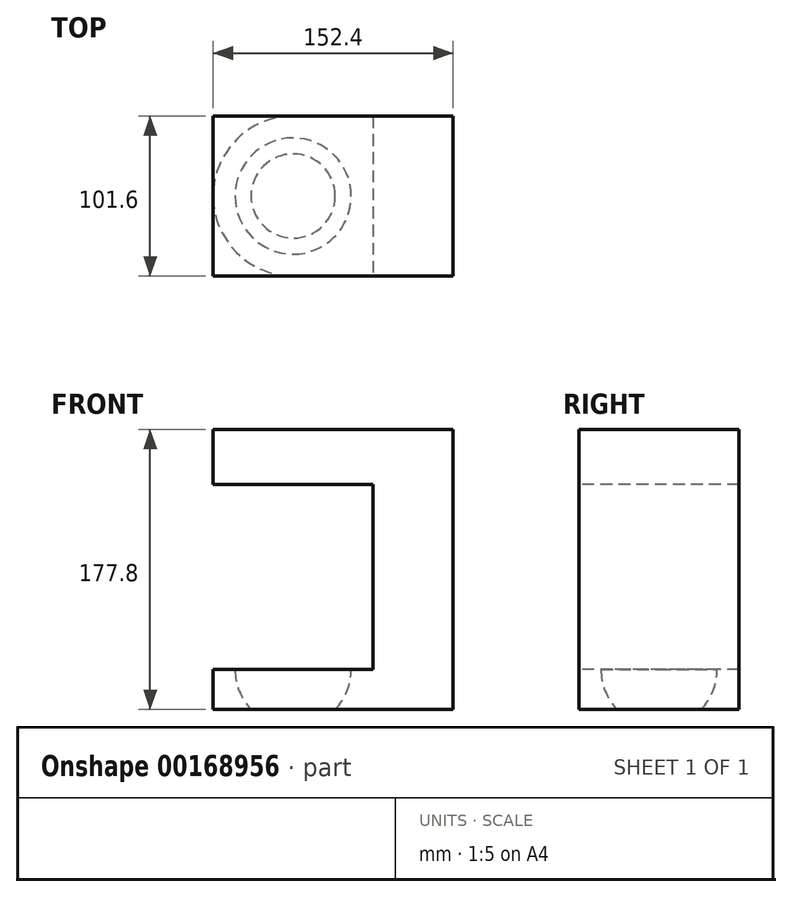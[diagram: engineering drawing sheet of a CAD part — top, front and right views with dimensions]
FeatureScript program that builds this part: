
annotation { "Feature Type Name" : "Feature", "Feature Type Description" : "" }
export const myFeature = defineFeature(function(context is Context, id is Id, definition is map)
    precondition{}
    {
        {
            var Q0;
            Q0=qCreatedBy(makeId("Top.planeOp"),FACE);
            var sketch = newSketch(context, id + "F0", { "sketchPlane" : qUnion([Q0])});
            skCircle(sketch, "E0", {"center": v(0, 0) * mm, "radius": 50.8 * mm});
            skLineSegment(sketch, "E1.bottom", {"start": v(0, 50.8) * mm, "end": v(101.6, 50.8) * mm});
            skLineSegment(sketch, "E1.top", {"start": v(0, -50.8) * mm, "end": v(101.6, -50.8) * mm});
            skLineSegment(sketch, "E1.left", {"start": v(0, 50.8) * mm, "end": v(0, -50.8) * mm});
            skLineSegment(sketch, "E1.right", {"start": v(101.6, 50.8) * mm, "end": v(101.6, -50.8) * mm});
            skSolve(sketch);
        }
        {
            var Q0;
            {var subQ0=sQuery(id+"F0.wireOp",EDGE,"E1.left");Q0=makeQuery(id+"F0.imprint","IMPRINT",FACE,{"disambiguationData":[TD([[makeQuery(id+"F0.imprint","IMPRINT",EDGE,{"derivedFrom":subQ0}),-1.0]])]});}
            var Q1;
            {var subQ0=sQuery(id+"F0.wireOp",EDGE,"E1.left");Q1=makeQuery(id+"F0.imprint","IMPRINT",FACE,{"disambiguationData":[TD([[makeQuery(id+"F0.imprint","IMPRINT",EDGE,{"derivedFrom":subQ0}),1.0]])]});}
            var Q2;
            {var subQ1=sQuery(id+"F0.wireOp",EDGE,"E1.bottom");Q2=makeQuery(id+"F0.imprint","IMPRINT",FACE,{"disambiguationData":[TD([[makeQuery(id+"F0.imprint","IMPRINT",EDGE,{"derivedFrom":subQ1}),-1.0]])]});}
            extrude(context, id + "F1", {"entities" : qUnion([Q0, Q1, Q2]), "depth" : 25.4 * mm});
        }
        {
            var Q0;
            Q0=makeQuery(id+"F1.opExtrude","CAP_FACE",FACE,{"disambiguationData":[OSD([sQuery(id+"F0.wireOp",EDGE,"E0"),sQuery(id+"F0.wireOp",EDGE,"E1.bottom"),sQuery(id+"F0.wireOp",EDGE,"E1.top"),sQuery(id+"F0.wireOp",EDGE,"E1.right")])],"isStart":false});
            var sketch = newSketch(context, id + "F2", { "sketchPlane" : qUnion([Q0])});
            skLineSegment(sketch, "E2.bottom", {"start": v(101.6, 50.8) * mm, "end": v(50.8, 50.8) * mm});
            skLineSegment(sketch, "E2.top", {"start": v(101.6, -50.8) * mm, "end": v(50.8, -50.8) * mm});
            skLineSegment(sketch, "E2.left", {"start": v(101.6, 50.8) * mm, "end": v(101.6, -50.8) * mm});
            skLineSegment(sketch, "E2.right", {"start": v(50.8, 50.8) * mm, "end": v(50.8, -50.8) * mm});
            skSolve(sketch);
        }
        {
            var Q0;
            Q0=makeQuery(id+"F2.imprint","IMPRINT",FACE,{"disambiguationData":[TD([[makeQuery(id+"F2.imprint","IMPRINT",EDGE,{"derivedFrom":sQuery(id+"F2.wireOp",EDGE,"E2.bottom")}),-1.0]])]});
            extrude(context, id + "F3", {"entities" : qUnion([Q0]), "operationType" : NewBodyOperationType.ADD, "depth" : 152.4 * mm});
        }
        {
            var Q0;
            Q0=makeQuery(id+"F1.opExtrude","CAP_FACE",FACE,{"disambiguationData":[OSD([sQuery(id+"F0.wireOp",EDGE,"E0"),sQuery(id+"F0.wireOp",EDGE,"E1.bottom"),sQuery(id+"F0.wireOp",EDGE,"E1.top"),sQuery(id+"F0.wireOp",EDGE,"E1.right")])],"isStart":false});
            var sketch = newSketch(context, id + "F4", { "sketchPlane" : qUnion([Q0])});
            skCircle(sketch, "E3", {"center": v(0, 0) * mm, "radius": 36.87 * mm});
            skLineSegment(sketch, "E4", {"start": v(0, -36.87) * mm, "end": v(0, 36.87) * mm});
            skSolve(sketch);
        }
        {
            var Q0;
            {var subQ0=sQuery(id+"F4.wireOp",EDGE,"E4");Q0=makeQuery(id+"F4.imprint","IMPRINT",FACE,{"disambiguationData":[TD([[makeQuery(id+"F4.imprint","IMPRINT",EDGE,{"derivedFrom":subQ0}),-1.0]])]});}
            var Q1;
            Q1=sQuery(id+"F4.wireOp",EDGE,"E4");
            revolve(context, id + "F5", {"entities" : qUnion([Q0]), "axis" : qUnion([Q1]), "revolveType" : RevolveType.FULL});
        }
        {
            var Q0;
            Q0=makeQuery(id+"F5.opRevolve","SWEPT_BODY",BODY,{"disambiguationData":[OSD([sQuery(id+"F4.wireOp",EDGE,"E3"),sQuery(id+"F4.wireOp",EDGE,"E4")])]});
            var Q1;
            Q1=makeQuery(id+"F1.opExtrude","SWEPT_BODY",BODY,{"disambiguationData":[OSD([sQuery(id+"F0.wireOp",EDGE,"E0"),sQuery(id+"F0.wireOp",EDGE,"E1.bottom"),sQuery(id+"F0.wireOp",EDGE,"E1.top"),sQuery(id+"F0.wireOp",EDGE,"E1.right")])]});
            booleanBodies(context, id + "F6", {"operationType" : BooleanOperationType.SUBTRACTION, "tools" : qUnion([Q0]), "targets" : qUnion([Q1])});
        }
        {
            var Q0;
            Q0=makeQuery(id+"F3.opExtrude","SWEPT_FACE",FACE,{"disambiguationData":[OSD([sQuery(id+"F2.wireOp",EDGE,"E2.right")])]});
            var sketch = newSketch(context, id + "F7", { "sketchPlane" : qUnion([Q0])});
            skLineSegment(sketch, "E5.bottom", {"start": v(-50.8, 177.8) * mm, "end": v(50.8, 177.8) * mm});
            skLineSegment(sketch, "E5.top", {"start": v(-50.8, 142.75) * mm, "end": v(50.8, 142.75) * mm});
            skLineSegment(sketch, "E5.left", {"start": v(-50.8, 177.8) * mm, "end": v(-50.8, 142.75) * mm});
            skLineSegment(sketch, "E5.right", {"start": v(50.8, 177.8) * mm, "end": v(50.8, 142.75) * mm});
            skSolve(sketch);
        }
        {
            var Q0;
            Q0=makeQuery(id+"F7.imprint","IMPRINT",FACE,{"disambiguationData":[TD([[makeQuery(id+"F7.imprint","IMPRINT",EDGE,{"derivedFrom":sQuery(id+"F7.wireOp",EDGE,"E5.bottom")}),-1.0]])]});
            extrude(context, id + "F8", {"entities" : qUnion([Q0]), "operationType" : NewBodyOperationType.ADD, "depth" : 101.6 * mm});
        }
    });
